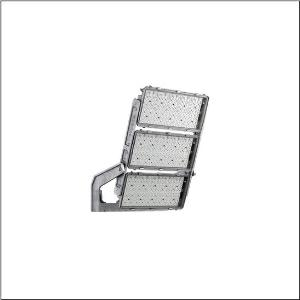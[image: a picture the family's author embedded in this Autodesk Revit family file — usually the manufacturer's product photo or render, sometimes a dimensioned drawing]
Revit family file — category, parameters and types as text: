
# Revit family: floodlight_fl_11_maxi_pro_remote___pl64blc_5xa779426w01aa_c02a
name_source: partatom
category: Lighting Fixtures
units: mm (PartAtom-declared; Revit-internal decimal feet)

## family parameters
Cut with Voids When Loaded = No
Host = Face
Light Source = No
Part Type = Normal
Room Calculation Point = No
Round Connector Dimension = Use Diameter
Shared = No

## types (1)
- --- (1 x LED, 140990 lm, 1516.9 W, 4000K)
    Apparent Load = 1517 VA
    CIE Flux Codes = 28 83 99 100 100
    Color Rendering = 70
    Color Temperature = 4000K
    Default Elevation = 1800 mm
    Description = Floodlight FL 11  maxi  pro Remote floodlight; light control with lens of PMMA; cover panel of toughened safety glass, transparent; light distribution: PL64BLC, asymmetric direct distribution, LEDcolour temperature: 4000K, rated luminous flux: 140.990lm, colour rendering: CRI > 70, light colour: 740; luminous efficacy: 93lm/W; brightness control: DALI 2 (1 DALI address); with terminal, 8-pole, max. 2.5mm², mains connection: 220..240V/380..400V AC, 50/60Hz, surge voltage resistance: line to ground: 10kV, ECG replaceable separately, no afterglow with DALI off / DMX off command, LED unit replaceable without ESD environment, dustproof LED module, dimming range 10..100%; 1517W floodlight with 2x LED unit of diecast aluminium, coated grey; length: 713mm / width: 651mm / height: 338mm; mounting bracket, of diecast aluminium, uncoated, natural, equipment: Power, protection rating (complete): IP66; insulation class (complete): insulation class I (protective earthing); certification: CE, ENEC, VDE; ball protection: ball impact resistance with accessories, impact resistance: IK07; only for outdoor installations, rated ambient temperature 10°C, permissible operating ambient temperature: -40..+30°C, permissible storage temperature: -40..+85°C; packaging unit: 1 piece

Light Distribution: PL64BLC
    Height = 320 mm
    Lamp = 1 x LED
    Lamp Light Flux = 140990 lm
    Lamp Power = 1516.9 W
    Lamp count = 1
    Length = 1002 mm
    Luminous efficacy = 93 lm/W
    Manufacturer = Siteco
    ModVariant = No
    Model = 5XA779426W01AA
    Mounting Place = Ceiling
    Mounting Type = Surface mounted
    Number of Poles = 1
    OnlyDefault = Yes
    Power Factor = 1
    Product Name = Floodlight FL 11 maxi pro Remote | PL64BLC
    Product group = floodlight | ceiling mounted
    ProductGroupID = 302
    Protection Class = Protection class I
    Protection Degree = IP 66
    RLX_Detail_Level = 1
    RLX_Emergency_Light_Flux = 0 lm
    RLX_Emergency_Type = 0
    RLX_Emergency_Type_DB = No
    RlxData = <blob elided: 52105 chars, md5=d55664e9>
    Socket = socket
    Standby Power = 0 W
    System Light Flux = 140990 lm
    System Power = 1517 W
    Type Comments = factory setting: luminous flux: 100 % | dim-lin: 254 | 1070 mA
    Type Image = l_1006784.jpg
    URL = http://relux.com
    VarID = @adj_050099
    Voltage = 0 V
    Weight = 0.00 kg
    Width = 655 mm

## geometry (parser evidence)
native form markers: Blend x4, Sweep x16
no freeform markers — native parametric forms only
